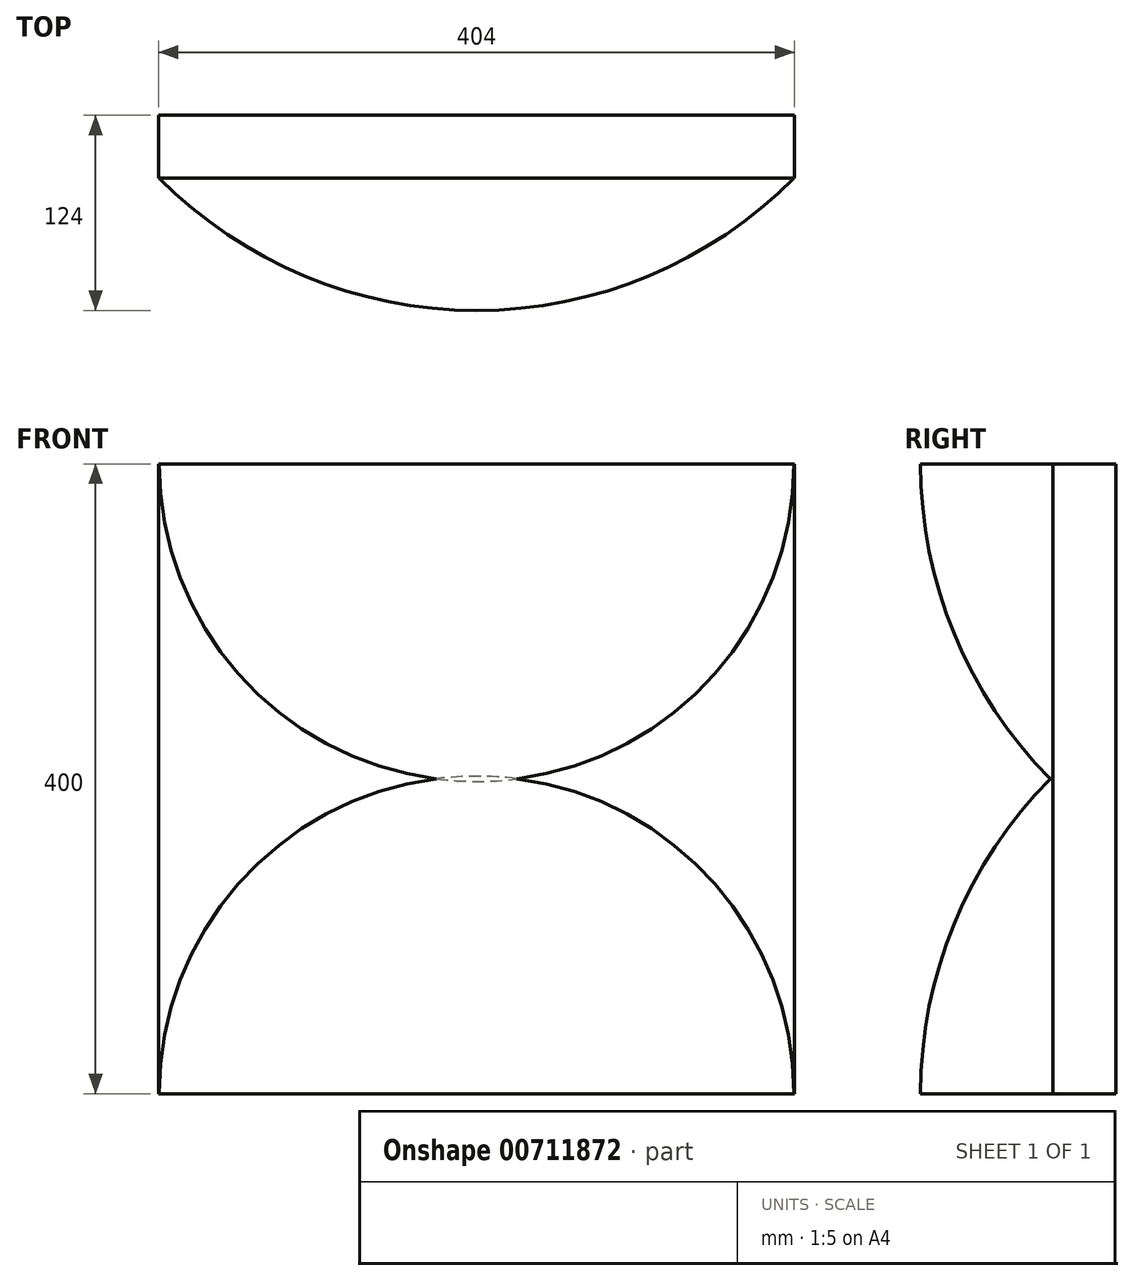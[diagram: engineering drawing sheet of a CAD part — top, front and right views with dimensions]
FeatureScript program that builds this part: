
annotation { "Feature Type Name" : "Feature", "Feature Type Description" : "" }
export const myFeature = defineFeature(function(context is Context, id is Id, definition is map)
    precondition{}
    {
        {
            var Q0;
            Q0=qCreatedBy(makeId("Front.planeOp"),FACE);
            var sketch = newSketch(context, id + "F0", { "sketchPlane" : qUnion([Q0])});
            skArc(sketch, "E0", {"start": v(284, 0) * mm, "mid": v(0, 284) * mm, "end": v(-284, 0) * mm});
            skPoint(sketch, "E1", {"position": v(-284, 0) * mm});
            skPoint(sketch, "E2", {"position": v(284, 0) * mm});
            skLineSegment(sketch, "E3", {"start": v(-284, 0) * mm, "end": v(284, 0) * mm});
            skSolve(sketch);
        }
        {
            var Q0;
            Q0=makeQuery(id+"F0.imprint","IMPRINT",FACE,{"disambiguationData":[TD([[makeQuery(id+"F0.imprint","IMPRINT",EDGE,{"derivedFrom":sQuery(id+"F0.wireOp",EDGE,"E0")}),1.0]])]});
            var Q1;
            Q1=sQuery(id+"F0.wireOp",EDGE,"E3");
            revolve(context, id + "F1", {"surfaceOperationType" : NewSurfaceOperationType.NEW, "entities" : qUnion([Q0]), "axis" : qUnion([Q1]), "revolveType" : RevolveType.FULL});
        }
        {
            var Q0;
            Q0=qCreatedBy(makeId("Front.planeOp"),FACE);
            cPlane(context, id + "F2", {"entities" : qUnion([Q0]), "cplaneType" : CPlaneType.OFFSET, "offset" : 200 * mm, "width" : 150 * mm, "height" : 150 * mm});
        }
        {
            var Q0;
            Q0=qCreatedBy(id+"F2.planeOp",FACE);
            var sketch = newSketch(context, id + "F3", { "sketchPlane" : qUnion([Q0])});
            skCircle(sketch, "E4", {"center": v(0, 0) * mm, "radius": 300 * mm});
            skSolve(sketch);
        }
        {
            var Q0;
            Q0=makeQuery(id+"F3.imprint","IMPRINT",FACE,{"disambiguationData":[TD([[makeQuery(id+"F3.imprint","IMPRINT",EDGE,{"derivedFrom":sQuery(id+"F3.wireOp",EDGE,"E4")}),1.0]])]});
            extrude(context, id + "F4", {"entities" : qUnion([Q0]), "operationType" : NewBodyOperationType.REMOVE, "oppositeDirection" : true, "depth" : 500 * mm, "offsetDistance" : 25 * mm});
        }
        {
            var Q0;
            Q0=makeQuery(id+"F1.opRevolve","SWEPT_BODY",BODY,{"disambiguationData":[OSD([sQuery(id+"F0.wireOp",EDGE,"E0"),sQuery(id+"F0.wireOp",EDGE,"E3")])]});
            transform(context, id + "F5", {"entities" : qUnion([Q0]), "transformType" : TransformType.TRANSLATION_3D, "dx" : 0 * mm, "dy" : 0 * mm, "dz" : 400 * mm, "makeCopy" : true});
        }
        {
            var Q0;
            Q0=qCreatedBy(id+"F2.planeOp",FACE);
            var sketch = newSketch(context, id + "F6", { "sketchPlane" : qUnion([Q0])});
            skLineSegment(sketch, "E5.bottom", {"start": v(-227.06, 0) * mm, "end": v(244.99, 0) * mm});
            skLineSegment(sketch, "E5.top", {"start": v(-227.06, 0) * mm, "end": v(244.99, 0) * mm});
            skLineSegment(sketch, "E5.left", {"start": v(-227.06, 0) * mm, "end": v(-227.06, 0) * mm});
            skLineSegment(sketch, "E5.right", {"start": v(244.99, 0) * mm, "end": v(244.99, 0) * mm});
            skLineSegment(sketch, "E6.bottom", {"start": v(244.99, -266.48) * mm, "end": v(-227.06, -266.48) * mm});
            skLineSegment(sketch, "E6.top", {"start": v(244.99, 0) * mm, "end": v(-227.06, 0) * mm});
            skLineSegment(sketch, "E6.left", {"start": v(244.99, -266.48) * mm, "end": v(244.99, 0) * mm});
            skLineSegment(sketch, "E6.right", {"start": v(-227.06, -266.48) * mm, "end": v(-227.06, 0) * mm});
            skSolve(sketch);
        }
        {
            var Q0;
            Q0=makeQuery(id+"F6.imprint","IMPRINT",FACE,{"disambiguationData":[TD([[makeQuery(id+"F6.imprint","IMPRINT",EDGE,{"derivedFrom":sQuery(id+"F6.wireOp",EDGE,"E6.bottom")}),-1.0]])]});
            extrude(context, id + "F7", {"entities" : qUnion([Q0]), "operationType" : NewBodyOperationType.REMOVE, "depth" : 90 * mm, "offsetDistance" : 25 * mm});
        }
        {
            var Q0;
            Q0=qCreatedBy(id+"F2.planeOp",FACE);
            var sketch = newSketch(context, id + "F8", { "sketchPlane" : qUnion([Q0])});
            skLineSegment(sketch, "E7.bottom", {"start": v(-223.84, 400) * mm, "end": v(235.18, 400) * mm});
            skLineSegment(sketch, "E7.top", {"start": v(-223.84, 631.32) * mm, "end": v(235.18, 631.32) * mm});
            skLineSegment(sketch, "E7.left", {"start": v(-223.84, 400) * mm, "end": v(-223.84, 631.32) * mm});
            skLineSegment(sketch, "E7.right", {"start": v(235.18, 400) * mm, "end": v(235.18, 631.32) * mm});
            skSolve(sketch);
        }
        {
            var Q0;
            Q0=makeQuery(id+"F8.imprint","IMPRINT",FACE,{"disambiguationData":[TD([[makeQuery(id+"F8.imprint","IMPRINT",EDGE,{"derivedFrom":sQuery(id+"F8.wireOp",EDGE,"E7.bottom")}),1.0]])]});
            extrude(context, id + "F9", {"entities" : qUnion([Q0]), "operationType" : NewBodyOperationType.REMOVE, "depth" : 90 * mm, "offsetDistance" : 25 * mm});
        }
        {
            var Q0;
            Q0=qCreatedBy(id+"F2.planeOp",FACE);
            var sketch = newSketch(context, id + "F10", { "sketchPlane" : qUnion([Q0])});
            skLineSegment(sketch, "E8.bottom", {"start": v(-202, 0) * mm, "end": v(202, 0) * mm});
            skLineSegment(sketch, "E8.top", {"start": v(-202, 0) * mm, "end": v(202, 0) * mm});
            skLineSegment(sketch, "E8.left", {"start": v(-202, 0) * mm, "end": v(-202, 0) * mm});
            skLineSegment(sketch, "E8.right", {"start": v(202, 0) * mm, "end": v(202, 0) * mm});
            skLineSegment(sketch, "E9.bottom", {"start": v(202, 400) * mm, "end": v(-202, 400) * mm});
            skLineSegment(sketch, "E9.top", {"start": v(202, 0) * mm, "end": v(-202, 0) * mm});
            skLineSegment(sketch, "E9.left", {"start": v(202, 400) * mm, "end": v(202, 0) * mm});
            skLineSegment(sketch, "E9.right", {"start": v(-202, 400) * mm, "end": v(-202, 0) * mm});
            skSolve(sketch);
        }
        {
            var Q0;
            Q0=makeQuery(id+"F10.imprint","IMPRINT",FACE,{"disambiguationData":[TD([[makeQuery(id+"F10.imprint","IMPRINT",EDGE,{"derivedFrom":sQuery(id+"F10.wireOp",EDGE,"E9.bottom")}),1.0]])]});
            extrude(context, id + "F11", {"entities" : qUnion([Q0]), "oppositeDirection" : true, "depth" : 40 * mm, "offsetDistance" : 25 * mm});
        }
    });
